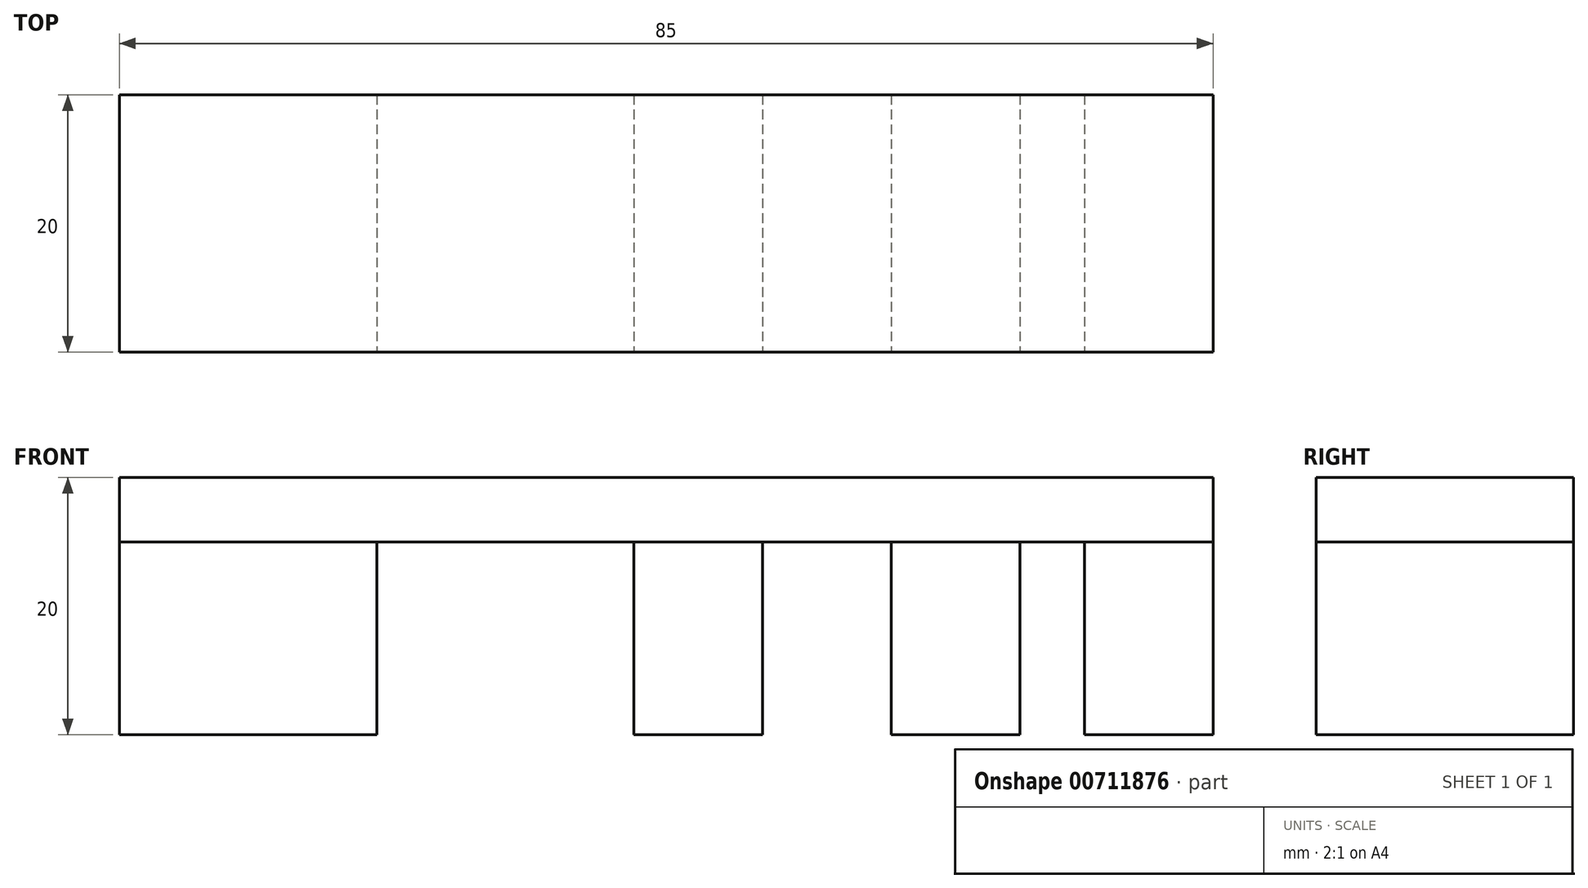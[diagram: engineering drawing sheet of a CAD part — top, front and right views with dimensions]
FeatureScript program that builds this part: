
annotation { "Feature Type Name" : "Feature", "Feature Type Description" : "" }
export const myFeature = defineFeature(function(context is Context, id is Id, definition is map)
    precondition{}
    {
        {
            var Q0;
            Q0=qCreatedBy(makeId("Top.planeOp"),FACE);
            var sketch = newSketch(context, id + "F0", { "sketchPlane" : qUnion([Q0])});
            skLineSegment(sketch, "E0.bottom", {"start": v(-43.32, -18.07) * mm, "end": v(-23.32, -18.07) * mm});
            skLineSegment(sketch, "E0.top", {"start": v(-43.32, -38.07) * mm, "end": v(-23.32, -38.07) * mm});
            skLineSegment(sketch, "E0.left", {"start": v(-43.32, -18.07) * mm, "end": v(-43.32, -38.07) * mm});
            skLineSegment(sketch, "E0.right", {"start": v(-23.32, -18.07) * mm, "end": v(-23.32, -38.07) * mm});
            skLineSegment(sketch, "E1.bottom", {"start": v(-3.32, -18.07) * mm, "end": v(6.68, -18.07) * mm});
            skLineSegment(sketch, "E1.top", {"start": v(-3.32, -38.07) * mm, "end": v(6.68, -38.07) * mm});
            skLineSegment(sketch, "E1.left", {"start": v(-3.32, -18.07) * mm, "end": v(-3.32, -38.07) * mm});
            skLineSegment(sketch, "E1.right", {"start": v(6.68, -18.07) * mm, "end": v(6.68, -38.07) * mm});
            skLineSegment(sketch, "E2.bottom", {"start": v(16.68, -18.07) * mm, "end": v(26.68, -18.07) * mm});
            skLineSegment(sketch, "E2.top", {"start": v(16.68, -38.07) * mm, "end": v(26.68, -38.07) * mm});
            skLineSegment(sketch, "E2.left", {"start": v(16.68, -18.07) * mm, "end": v(16.68, -38.07) * mm});
            skLineSegment(sketch, "E2.right", {"start": v(26.68, -18.07) * mm, "end": v(26.68, -38.07) * mm});
            skPoint(sketch, "E3.firstSnap0", {"position": v(21.68, -18.07) * mm});
            skLineSegment(sketch, "E3.bottom", {"start": v(31.68, -18.07) * mm, "end": v(41.68, -18.07) * mm});
            skLineSegment(sketch, "E3.top", {"start": v(31.68, -38.07) * mm, "end": v(41.68, -38.07) * mm});
            skLineSegment(sketch, "E3.left", {"start": v(31.68, -18.07) * mm, "end": v(31.68, -38.07) * mm});
            skLineSegment(sketch, "E3.right", {"start": v(41.68, -18.07) * mm, "end": v(41.68, -38.07) * mm});
            skSolve(sketch);
        }
        {
            var Q0;
            Q0=makeQuery(id+"F0.imprint","IMPRINT",FACE,{"disambiguationData":[TD([[makeQuery(id+"F0.imprint","IMPRINT",EDGE,{"derivedFrom":sQuery(id+"F0.wireOp",EDGE,"E0.bottom")}),-1.0]])]});
            var Q1;
            Q1=makeQuery(id+"F0.imprint","IMPRINT",FACE,{"disambiguationData":[TD([[makeQuery(id+"F0.imprint","IMPRINT",EDGE,{"derivedFrom":sQuery(id+"F0.wireOp",EDGE,"E1.bottom")}),-1.0]])]});
            var Q2;
            Q2=makeQuery(id+"F0.imprint","IMPRINT",FACE,{"disambiguationData":[TD([[makeQuery(id+"F0.imprint","IMPRINT",EDGE,{"derivedFrom":sQuery(id+"F0.wireOp",EDGE,"E2.bottom")}),-1.0]])]});
            var Q3;
            Q3=makeQuery(id+"F0.imprint","IMPRINT",FACE,{"disambiguationData":[TD([[makeQuery(id+"F0.imprint","IMPRINT",EDGE,{"derivedFrom":sQuery(id+"F0.wireOp",EDGE,"E3.bottom")}),-1.0]])]});
            extrude(context, id + "F1", {"entities" : qUnion([Q0, Q1, Q2, Q3]), "depth" : 15 * mm, "offsetDistance" : 25 * mm});
        }
        {
            var Q0;
            Q0=makeQuery(id+"F1.opExtrude","CAP_FACE",FACE,{"disambiguationData":[OSD([sQuery(id+"F0.wireOp",EDGE,"E0.bottom"),sQuery(id+"F0.wireOp",EDGE,"E0.top"),sQuery(id+"F0.wireOp",EDGE,"E0.left"),sQuery(id+"F0.wireOp",EDGE,"E0.right")])],"isStart":false});
            var sketch = newSketch(context, id + "F2", { "sketchPlane" : qUnion([Q0])});
            skLineSegment(sketch, "E4.bottom", {"start": v(-43.32, -18.07) * mm, "end": v(41.68, -18.07) * mm});
            skLineSegment(sketch, "E4.top", {"start": v(-43.32, -38.07) * mm, "end": v(41.68, -38.07) * mm});
            skLineSegment(sketch, "E4.left", {"start": v(-43.32, -18.07) * mm, "end": v(-43.32, -38.07) * mm});
            skLineSegment(sketch, "E4.right", {"start": v(41.68, -18.07) * mm, "end": v(41.68, -38.07) * mm});
            skSolve(sketch);
        }
        {
            var Q0;
            {var subQ2=sQuery(id+"F2.wireOp",EDGE,"E4.right");Q0=makeQuery(id+"F2.imprint","IMPRINT",FACE,{"disambiguationData":[TD([[makeQuery(id+"F2.imprint","IMPRINT",EDGE,{"derivedFrom":subQ2}),-1.0]])]});}
            var Q1;
            {var subQ0=sQuery(id+"F2.wireOp",EDGE,"E4.left");Q1=makeQuery(id+"F2.imprint","IMPRINT",FACE,{"disambiguationData":[TD([[makeQuery(id+"F2.imprint","IMPRINT",EDGE,{"derivedFrom":subQ0}),1.0]])]});}
            extrude(context, id + "F3", {"entities" : qUnion([Q0, Q1]), "depth" : 5 * mm, "offsetDistance" : 25 * mm});
        }
    });
